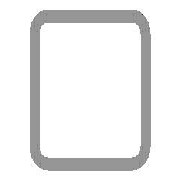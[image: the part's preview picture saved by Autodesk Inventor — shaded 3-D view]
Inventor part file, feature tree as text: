
AUTODESK INVENTOR PART (.ipt)
format: ipt  version: 2024.3 (Build 283343000, 343)  size: 139,776 bytes
history: native  units: mm (DEFAULTED — no unit token found)
features: other x4, plane x2, split x1, sketch x1
ambient origin geometry x8: Origin, YZ Plane, XZ Plane, XY Plane, X Axis, Y Axis, Z Axis, Center Point
bodies: Solid1 (feature_tree), Body (feature_tree)
feature tree (8):
  parser-record x1  (decoder bookkeeping rows leaked as tree rows — omitted from the tree; the rows remain in map.json)
  other  "Driven Length"
  other  "Start Plane"
  other  "End Plane"
  plane  "Work Plane4"
  split  "Split1"
  sketch  "Sketch3"  dims[d3=90.0mm d4=0.0mm d7=4.0mm d9=20.0mm d11=20.0mm d12=2.0mm d13=-0.0mm d14=90.0mm d15=10.0mm d16=10.0mm d17=90.0deg d18=90.0mm]
  plane  "Work Plane3"
